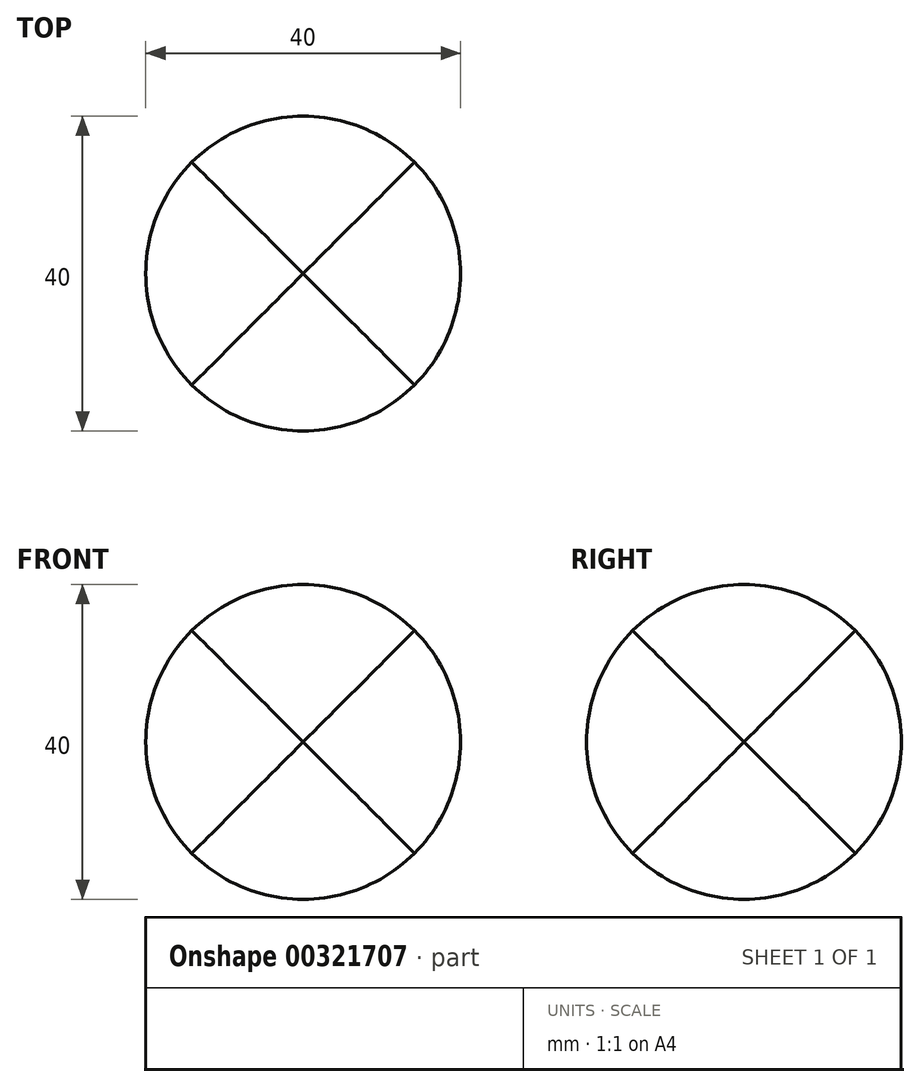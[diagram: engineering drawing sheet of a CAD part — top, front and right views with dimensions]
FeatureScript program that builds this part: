
annotation { "Feature Type Name" : "Feature", "Feature Type Description" : "" }
export const myFeature = defineFeature(function(context is Context, id is Id, definition is map)
    precondition{}
    {
        {
            var Q0;
            Q0=qCreatedBy(makeId("Front.planeOp"),FACE);
            var sketch = newSketch(context, id + "F0", { "sketchPlane" : qUnion([Q0])});
            skCircle(sketch, "E0", {"center": v(0, 0) * mm, "radius": 20 * mm});
            skSolve(sketch);
        }
        {
            var Q0;
            Q0=makeQuery(id+"F0.imprint","IMPRINT",FACE,{"disambiguationData":[TD([[makeQuery(id+"F0.imprint","IMPRINT",EDGE,{"derivedFrom":sQuery(id+"F0.wireOp",EDGE,"E0")}),1.0]])]});
            extrude(context, id + "F1", {"entities" : qUnion([Q0]), "endBound" : BoundingType.SYMMETRIC, "depth" : 50 * mm, "offsetDistance" : 25 * mm});
        }
        {
            var Q0;
            Q0=qCreatedBy(makeId("Front.planeOp"),FACE);
            var Q1;
            Q1=qCreatedBy(makeId("Right.planeOp"),FACE);
            cPlane(context, id + "F2", {"entities" : qUnion([Q0, Q1]), "cplaneType" : CPlaneType.MID_PLANE, "offset" : 25 * mm, "width" : 150 * mm, "height" : 150 * mm});
        }
        {
            var Q0;
            Q0=qCreatedBy(id+"F2.planeOp",FACE);
            var sketch = newSketch(context, id + "F3", { "sketchPlane" : qUnion([Q0])});
            skLineSegment(sketch, "E1", {"start": v(0, 0) * mm, "end": v(28.28, 20) * mm});
            skSolve(sketch);
        }
        {
            var Q0;
            Q0=makeQuery(id+"F1.opExtrude","SWEPT_BODY",BODY,{"disambiguationData":[OSD([sQuery(id+"F0.wireOp",EDGE,"E0")])]});
            var Q1;
            Q1=sQuery(id+"F3.wireOp",EDGE,"E1");
            circularPattern(context, id + "F4", {"entities" : qUnion([Q0]), "axis" : qUnion([Q1]), "angle" : 360 * degree, "instanceCount" : 3, "oppositeDirection" : true, "equalSpace" : true});
        }
        {
            var Q0;
            Q0=makeQuery(id+"F4.opPattern","COPY",BODY,{"derivedFrom":makeQuery(id+"F1.opExtrude","SWEPT_BODY",BODY,{"disambiguationData":[OSD([sQuery(id+"F0.wireOp",EDGE,"E0")])]}),"instanceName":"1"});
            var Q1;
            Q1=makeQuery(id+"F1.opExtrude","SWEPT_BODY",BODY,{"disambiguationData":[OSD([sQuery(id+"F0.wireOp",EDGE,"E0")])]});
            var Q2;
            Q2=makeQuery(id+"F4.opPattern","COPY",BODY,{"derivedFrom":makeQuery(id+"F1.opExtrude","SWEPT_BODY",BODY,{"disambiguationData":[OSD([sQuery(id+"F0.wireOp",EDGE,"E0")])]}),"instanceName":"2"});
            booleanBodies(context, id + "F5", {"operationType" : BooleanOperationType.INTERSECTION, "tools" : qUnion([Q0, Q1, Q2])});
        }
    });
